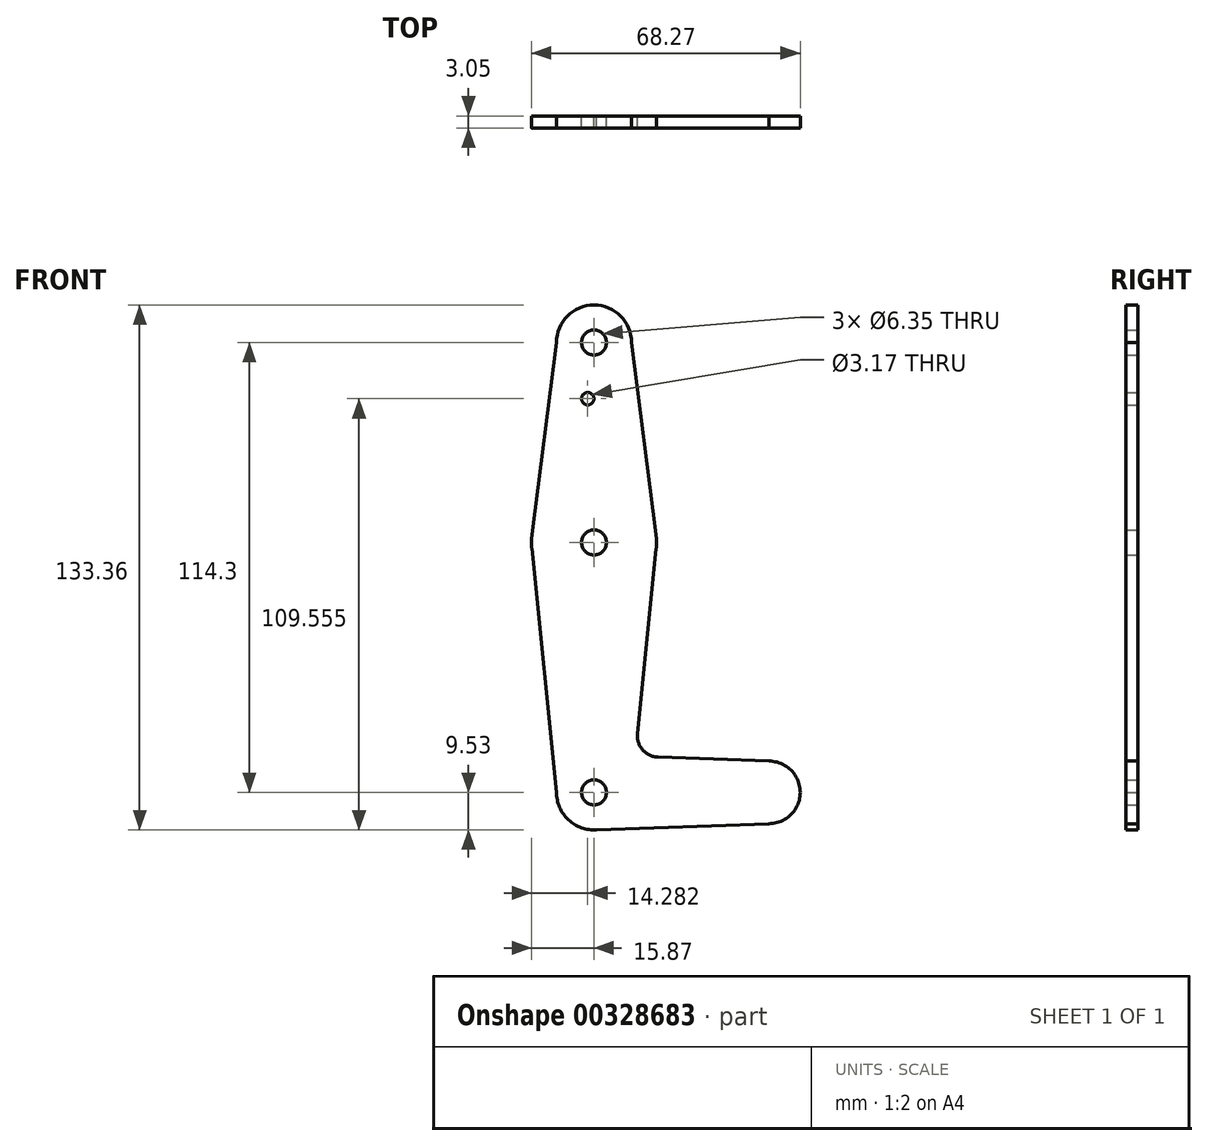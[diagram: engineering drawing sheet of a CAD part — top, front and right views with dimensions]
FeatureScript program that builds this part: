
annotation { "Feature Type Name" : "Feature", "Feature Type Description" : "" }
export const myFeature = defineFeature(function(context is Context, id is Id, definition is map)
    precondition{}
    {
        {
            var Q0;
            Q0=qCreatedBy(makeId("Front.planeOp"),FACE);
            var sketch = newSketch(context, id + "F0", { "sketchPlane" : qUnion([Q0])});
            skLineSegment(sketch, "E0", {"start": v(0, 0) * mm, "end": v(0, 114.3) * mm, "construction": true});
            skLineSegment(sketch, "E1", {"start": v(0, 0) * mm, "end": v(44.45, 0) * mm});
            skCircle(sketch, "E2", {"center": v(0, 114.3) * mm, "radius": 9.53 * mm});
            skCircle(sketch, "E3", {"center": v(0, 63.5) * mm, "radius": 15.88 * mm});
            skCircle(sketch, "E4", {"center": v(44.45, 0) * mm, "radius": 7.95 * mm});
            skCircle(sketch, "E5", {"center": v(0, 0) * mm, "radius": 9.53 * mm});
            skLineSegment(sketch, "E6", {"start": v(-9.53, 114.3) * mm, "end": v(-15.75, 65.5) * mm});
            skLineSegment(sketch, "E7", {"start": v(9.53, 114.3) * mm, "end": v(15.75, 65.5) * mm});
            skLineSegment(sketch, "E8", {"start": v(15.8, 61.91) * mm, "end": v(11.07, 14.9) * mm});
            skLineSegment(sketch, "E9", {"start": v(-15.8, 61.91) * mm, "end": v(-9.57, 0) * mm});
            skLineSegment(sketch, "E10", {"start": v(-9.57, 0) * mm, "end": v(-9.52, 0.05) * mm});
            skPoint(sketch, "E11.orphan", {"position": v(0, 9.53) * mm});
            skLineSegment(sketch, "E12", {"start": v(16.26, 8.95) * mm, "end": v(44.45, 7.96) * mm});
            skLineSegment(sketch, "E13", {"start": v(0, -9.53) * mm, "end": v(44.45, -7.95) * mm});
            skLineSegment(sketch, "E14", {"start": v(44.43, 7.95) * mm, "end": v(44.45, 7.96) * mm});
            skArc(sketch, "E15.filletArc", {"start": v(11.07, 14.9) * mm, "mid": v(12.38, 10.8) * mm, "end": v(16.26, 8.95) * mm});
            skCircle(sketch, "E16", {"center": v(-1.59, 100.03) * mm, "radius": 1.59 * mm});
            skCircle(sketch, "E17", {"center": v(0, 63.5) * mm, "radius": 3.18 * mm});
            skCircle(sketch, "E18", {"center": v(0, 114.3) * mm, "radius": 3.18 * mm});
            skCircle(sketch, "E19", {"center": v(0, 0) * mm, "radius": 3.18 * mm});
            skSolve(sketch);
        }
        {
            var Q0;
            Q0 = qSketchRegion(id + "F0", true);
            extrude(context, id + "F1", {"entities" : qUnion([Q0]), "depth" : 3.05 * mm});
        }
    });
